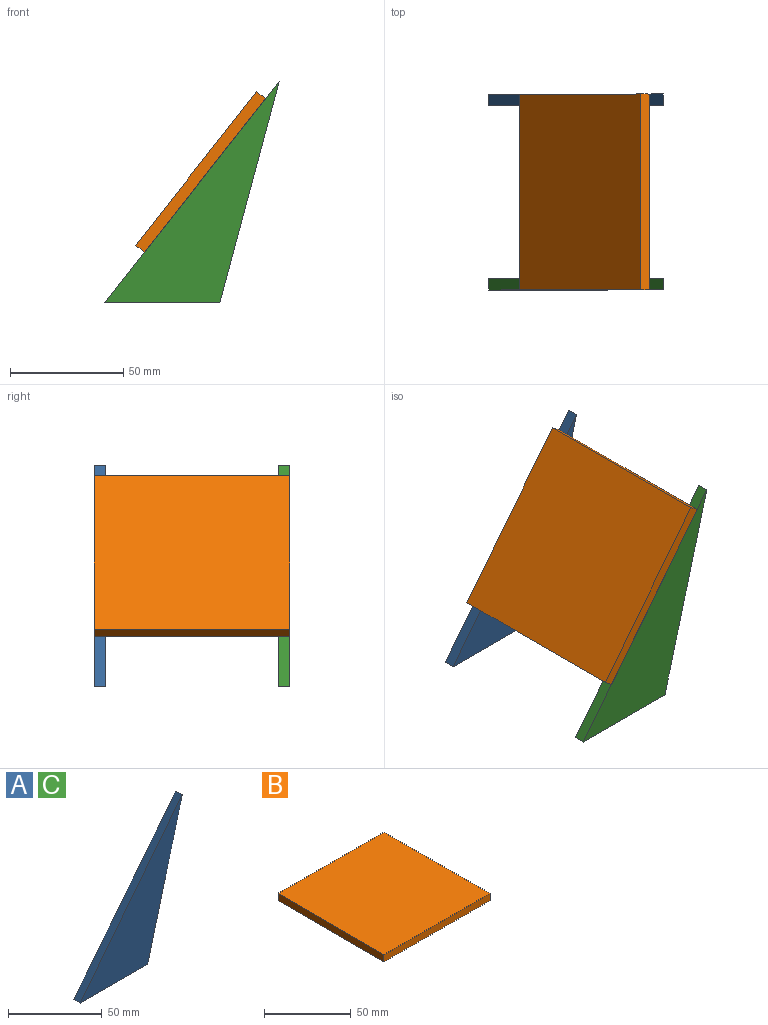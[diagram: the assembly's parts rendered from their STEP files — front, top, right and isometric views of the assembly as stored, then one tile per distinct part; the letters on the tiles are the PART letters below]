
ASSEMBLY  parts=3 mates=5
PART A: 5 faces, bbox 77x5x97.8 mm
  f0: plane 97.78x26.2mm, normal (0.97,0,-0.26), area 506.2mm2, adj f1,f2,f3,f4
  f1: plane 97.78x77mm, normal (-0.79,0,0.62), area 622.3mm2, adj f0,f2,f3,f4
  f2: plane 50.8x5mm, normal (0,0,-1), area 254mm2, adj f0,f1,f3,f4
  f3: plane 97.78x77mm, normal (0,-1,0), area 2483.6mm2, adj f0,f1,f2
  f4: plane 97.78x77mm, normal (0,1,0), area 2483.6mm2, adj f0,f1,f2
PART B: 6 faces, bbox 86.4x86.4x5 mm
  f0: plane 86.36x5mm, normal (0,-1,0), area 431.8mm2, adj f1,f3,f4,f5
  f1: plane 86.36x5mm, normal (1,0,0), area 431.8mm2, adj f0,f2,f4,f5
  f2: plane 86.36x5mm, normal (0,1,0), area 431.8mm2, adj f1,f3,f4,f5
  f3: plane 86.36x5mm, normal (-1,0,0), area 431.8mm2, adj f0,f2,f4,f5
  f4: plane 86.36x86.36mm, normal (0,0,1), area 7458mm2, adj f0,f1,f2,f3
  f5: plane 86.36x86.36mm, normal (0,0,-1), area 7458mm2, adj f0,f1,f2,f3
PART C: same geometry as A
PLACE A t=(13.74,56.1,-40.11)mm
PLACE B rot(axis=(0,-1,0),51.8deg) t=(57.99,12.92,16.08)mm
PLACE C t=(13.74,-25.26,-40.11)mm
MATE planar B.f5 <-> A.f1  axis (0.79,0,-0.62) through (57.99,12.92,16.08)mm
MATE planar B.f5 <-> C.f1  axis (0.79,0,-0.62) through (57.99,12.92,16.08)mm
MATE planar A.f4 <-> B.f2  axis (0,1,0) through (56.34,56.1,-7.52)mm
MATE planar C.f3 <-> B.f0  axis (0,-1,0) through (56.34,-30.26,-7.52)mm
MATE planar C.f2 <-> A.f2  axis (0,0,-1) through (39.14,-27.76,-40.11)mm
